# Revit family: Enclosure_System-CityScapes-Covrit-1313
name_source: partatom
category: Specialty Equipment
units: mm (PartAtom-declared; Revit-internal decimal feet)

## family parameters
Always vertical = Yes
Cut with Voids When Loaded = No
Part Type = Normal
Room Calculation Point = No
Round Connector Dimension = Use Diameter
Shared = No
Work Plane-Based = No

## types (3) — shared parameters
CAD Details = https://www.arcat.com
Default Elevation = 0' - 0"
Description = Dumpster Enclosure, Single
Keynote = 32 35 00
Length = 13' - 0"
Manufacturer = CityScapes
Model = Covrit 1313
Product Page URL = https://www.arcat.com
Specification = https://www.arcat.com
URL = https://cityscapesinc.com
Width = 13' - 0"

## per-type parameters (varying)
| type | Height | Post Height |
| 6' Height | 6' - 0" | Square_Post-Covrit-CityScapes : Square Post 6' |
| 7' Height | 7' - 0" | Square_Post-Covrit-CityScapes : Square Post 7' |
| 8' Height | 8' - 0" | Square_Post-Covrit-CityScapes : Square Post 8' |

## geometry (parser evidence)
native form markers: Sweep x16
no freeform markers — native parametric forms only
